# Revit family: HARMANN - AirDot 200
name_source: partatom
category: Mechanical Equipment
units: mm (PartAtom-declared; Revit-internal decimal feet)

## family parameters
Classification = None
Cut with Voids When Loaded = No
Host = Face
Maintain Annotation Orientation = No
Part Type = Normal
Room Calculation Point = No
Round Connector Dimension = Use Diameter
Shared = No

## types (2) — shared parameters
Autor = https://www.archispace.com
Ciśnienie akustyczne nominalne I Lpa = 21 dB(A)
Ciśnienie akustyczne nominalne II Lpa = 22 dB(A)
Ciśnienie akustyczne nominalne III Lpa = 32 dB(A)
Description = Rekuperatory ścienny
Kierunek przepływu = Dwukierunkowy
Maksymalna  Temperatura pracy Tmax = 50 °C
Manufacturer = Harmann Polska Sp. z o.o.
Masa = 5.00 kg
Otwór montażowy = 200 mm  [stored 0.656168 ft]
Powietrze Przepływ I bieg Qmax = 144.0 m³/h
Powietrze Przepływ II bieg Qmax = 252.0 m³/h
Powietrze Przepływ III bieg Qmax = 360.0 m³/h
Powietrze ciśnienie statyczne maksymalne I dPmax = 21.0 Pa
Powietrze ciśnienie statyczne maksymalne II dPmax = 32.0 Pa
Powietrze ciśnienie statyczne maksymalne III dPmax = 49.0 Pa
Zasilanie Częstotliwość Nominalna = 50 Hz
Zasilanie Ilość faz = 1
Zasilanie Moc maksymalna I bieg Pmax = 7 VA
Zasilanie Moc maksymalna II bieg Pmax = 10 VA
Zasilanie Moc maksymalna III bieg Pmax = 12 VA
Zasilanie Rodzaj Sterowania = III biegi
Zasilanie napięcie nominalne Unom = 230 V
Zasilanie natężenie maksymalne III biegi Imax = 0 A
Średnica = 195 mm  [stored 0.639764 ft]
zero-valued in all types: Default Elevation

## per-type parameters (varying)
| type | Numer artykułu |
| AIRDOT 200 link | 72251665 |
| AIRDOT 200 link+ | 72251668 |

note: column(s) folded — value = type name in every type: Model

note: [stored X ft] marks values corroborated as IEEE doubles in the binary element streams (Revit-internal decimal feet)

## geometry (parser evidence)
native form markers: Sweep x3
no freeform markers — native parametric forms only
